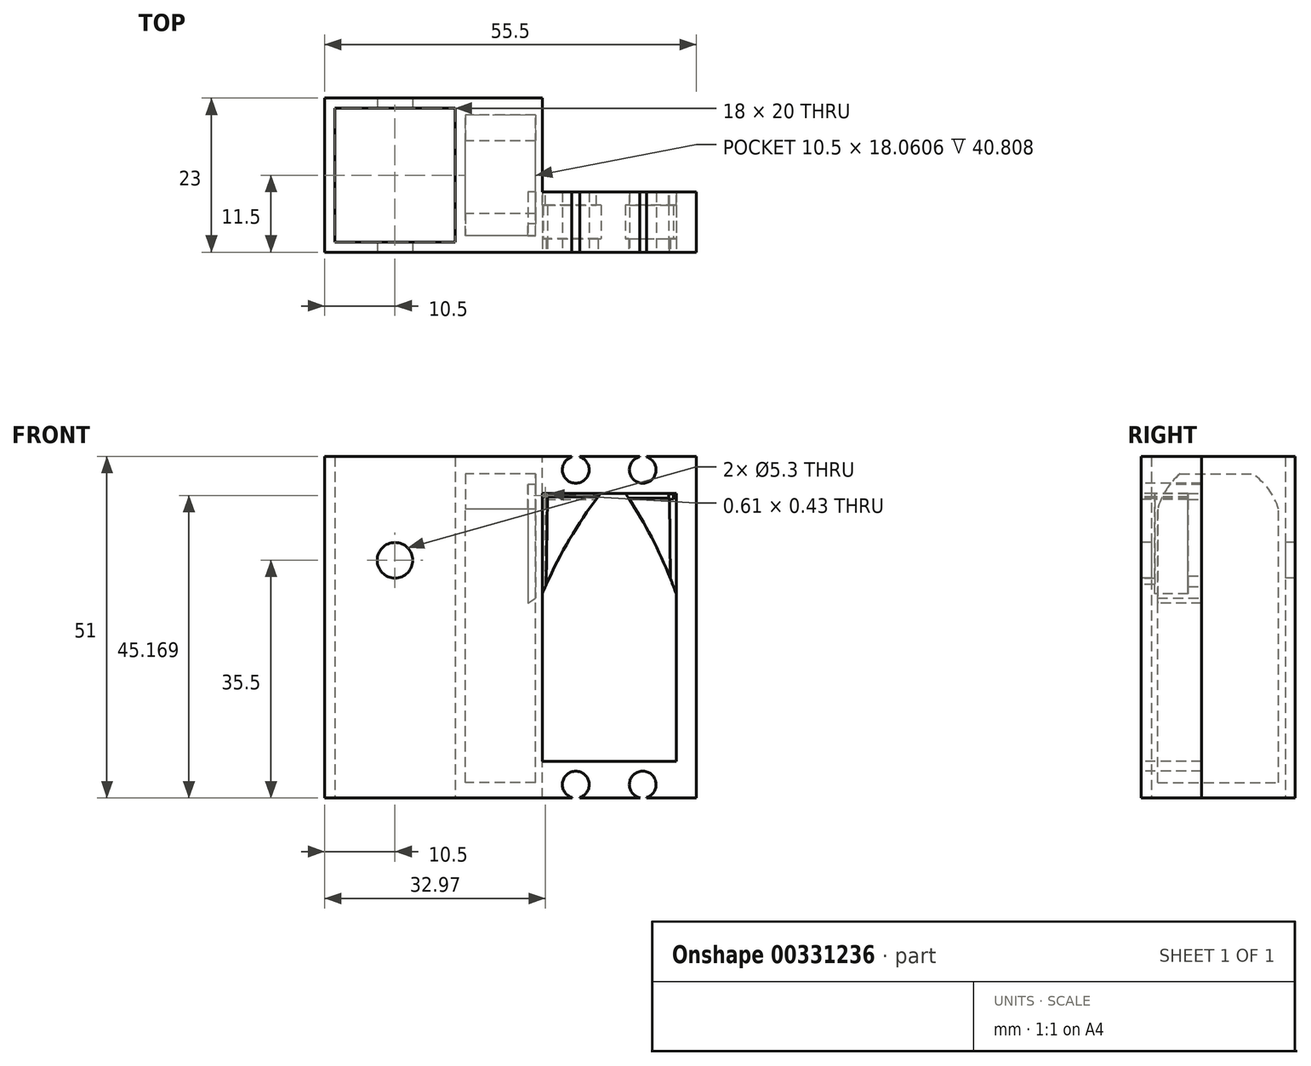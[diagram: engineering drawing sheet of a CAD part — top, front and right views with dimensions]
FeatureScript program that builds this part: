
annotation { "Feature Type Name" : "Feature", "Feature Type Description" : "" }
export const myFeature = defineFeature(function(context is Context, id is Id, definition is map)
    precondition{}
    {
        {
            var Q0;
            Q0=qCreatedBy(makeId("Top.planeOp"),FACE);
            var sketch = newSketch(context, id + "F0", { "sketchPlane" : qUnion([Q0])});
            skLineSegment(sketch, "E0.bottom", {"start": v(-9, -10) * mm, "end": v(9, -10) * mm});
            skLineSegment(sketch, "E0.top", {"start": v(-9, 10) * mm, "end": v(9, 10) * mm});
            skLineSegment(sketch, "E0.left", {"start": v(-9, -10) * mm, "end": v(-9, 10) * mm});
            skLineSegment(sketch, "E0.right", {"start": v(9, -10) * mm, "end": v(9, 10) * mm});
            skPoint(sketch, "E0.middle", {"position": v(0, 0) * mm});
            skLineSegment(sketch, "E1.bottom", {"start": v(-10.5, -11.5) * mm, "end": v(10.5, -11.5) * mm});
            skLineSegment(sketch, "E1.top", {"start": v(-10.5, 11.5) * mm, "end": v(10.5, 11.5) * mm});
            skLineSegment(sketch, "E1.left", {"start": v(-10.5, -11.5) * mm, "end": v(-10.5, 11.5) * mm});
            skLineSegment(sketch, "E1.right", {"start": v(10.5, -11.5) * mm, "end": v(10.5, 11.5) * mm});
            skSolve(sketch);
        }
        {
            var Q0;
            Q0 = qSketchRegion(id + "F0", true);
            extrude(context, id + "F1", {"entities" : qUnion([Q0]), "depth" : 51 * mm});
        }
        {
            var Q0;
            Q0=makeQuery(id+"F1.opExtrude","SWEPT_FACE",FACE,{"disambiguationData":[OSD([sQuery(id+"F0.wireOp",EDGE,"E1.right")])]});
            var sketch = newSketch(context, id + "F2", { "sketchPlane" : qUnion([Q0])});
            skLineSegment(sketch, "E2", {"start": v(-11.5, 51) * mm, "end": v(-11.5, 49) * mm});
            skLineSegment(sketch, "E3.bottom", {"start": v(-11.5, 51) * mm, "end": v(11.5, 51) * mm});
            skLineSegment(sketch, "E3.top", {"start": v(-11.5, 0) * mm, "end": v(11.5, 0) * mm});
            skLineSegment(sketch, "E3.left", {"start": v(-11.5, 51) * mm, "end": v(-11.5, 0) * mm});
            skLineSegment(sketch, "E3.right", {"start": v(11.5, 51) * mm, "end": v(11.5, 0) * mm});
            skLineSegment(sketch, "E4.bottom", {"start": v(-9.06, 2.33) * mm, "end": v(9, 2.33) * mm});
            skLineSegment(sketch, "E4.top", {"start": v(-9.06, 48.4) * mm, "end": v(9, 48.4) * mm});
            skLineSegment(sketch, "E4.left", {"start": v(-9.06, 2.33) * mm, "end": v(-9.06, 48.4) * mm});
            skLineSegment(sketch, "E4.right", {"start": v(9, 2.33) * mm, "end": v(9, 48.4) * mm});
            skArc(sketch, "E5", {"start": v(-5.75, 48.4) * mm, "mid": v(-7.8, 46) * mm, "end": v(-9.06, 43.13) * mm});
            skArc(sketch, "E6", {"start": v(9, 43.13) * mm, "mid": v(7.51, 46.1) * mm, "end": v(5.11, 48.4) * mm});
            skSolve(sketch);
        }
        {
            var Q0;
            Q0 = qSketchRegion(id + "F2", true);
            var Q1;
            {var subQ3=sQuery(id+"F2.wireOp",EDGE,"E5");Q1=makeQuery(id+"F2.imprint","IMPRINT",FACE,{"disambiguationData":[TD([[makeQuery(id+"F2.imprint","IMPRINT",EDGE,{"derivedFrom":subQ3}),-1.0]])]});}
            var Q2;
            {var subQ3=sQuery(id+"F2.wireOp",EDGE,"E6");Q2=makeQuery(id+"F2.imprint","IMPRINT",FACE,{"disambiguationData":[TD([[makeQuery(id+"F2.imprint","IMPRINT",EDGE,{"derivedFrom":subQ3}),-1.0]])]});}
            extrude(context, id + "F3", {"entities" : qUnion([Q0, Q1, Q2]), "operationType" : NewBodyOperationType.ADD, "depth" : 11.5 * mm});
        }
        {
            var Q0;
            Q0=makeQuery(id+"F3.opExtrude","CAP_FACE",FACE,{"disambiguationData":[OSD([sQuery(id+"F2.wireOp",EDGE,"E3.bottom"),sQuery(id+"F2.wireOp",EDGE,"E3.top"),sQuery(id+"F2.wireOp",EDGE,"E3.left"),sQuery(id+"F2.wireOp",EDGE,"E3.right"),sQuery(id+"F2.wireOp",EDGE,"E4.bottom"),sQuery(id+"F2.wireOp",EDGE,"E4.top"),sQuery(id+"F2.wireOp",EDGE,"E4.left"),sQuery(id+"F2.wireOp",EDGE,"E4.right"),sQuery(id+"F2.wireOp",EDGE,"E5"),sQuery(id+"F2.wireOp",EDGE,"E6")])],"isStart":false});
            var sketch = newSketch(context, id + "F4", { "sketchPlane" : qUnion([Q0])});
            skLineSegment(sketch, "E7.bottom", {"start": v(-11.5, 51) * mm, "end": v(11.5, 51) * mm});
            skLineSegment(sketch, "E7.top", {"start": v(-11.5, 0) * mm, "end": v(11.5, 0) * mm});
            skLineSegment(sketch, "E7.left", {"start": v(-11.5, 51) * mm, "end": v(-11.5, 0) * mm});
            skLineSegment(sketch, "E7.right", {"start": v(11.5, 51) * mm, "end": v(11.5, 0) * mm});
            skSolve(sketch);
        }
        {
            var Q0;
            Q0 = qSketchRegion(id + "F4", true);
            extrude(context, id + "F5", {"entities" : qUnion([Q0]), "operationType" : NewBodyOperationType.ADD, "oppositeDirection" : true, "depth" : 1 * mm});
        }
        {
            var Q0;
            Q0=makeQuery(id+"F5.boolean.opBoolean","MERGE",FACE,{"derivedFrom":[makeQuery(id+"F3.opExtrude","CAP_FACE",FACE,{"disambiguationData":[OSD([sQuery(id+"F2.wireOp",EDGE,"E3.bottom"),sQuery(id+"F2.wireOp",EDGE,"E3.top"),sQuery(id+"F2.wireOp",EDGE,"E3.left"),sQuery(id+"F2.wireOp",EDGE,"E3.right"),sQuery(id+"F2.wireOp",EDGE,"E4.bottom"),sQuery(id+"F2.wireOp",EDGE,"E4.top"),sQuery(id+"F2.wireOp",EDGE,"E4.left"),sQuery(id+"F2.wireOp",EDGE,"E4.right"),sQuery(id+"F2.wireOp",EDGE,"E5"),sQuery(id+"F2.wireOp",EDGE,"E6")])],"isStart":false}),makeQuery(id+"F5.opExtrude","CAP_FACE",FACE,{"disambiguationData":[OSD([sQuery(id+"F4.wireOp",EDGE,"E7.bottom"),sQuery(id+"F4.wireOp",EDGE,"E7.top"),sQuery(id+"F4.wireOp",EDGE,"E7.left"),sQuery(id+"F4.wireOp",EDGE,"E7.right")])],"isStart":true})]});
            var sketch = newSketch(context, id + "F6", { "sketchPlane" : qUnion([Q0])});
            skLineSegment(sketch, "E8", {"start": v(-11.5, 51) * mm, "end": v(-11.5, 49) * mm});
            skLineSegment(sketch, "E9", {"start": v(-11.5, 49) * mm, "end": v(-2.5, 49) * mm});
            skLineSegment(sketch, "E10", {"start": v(11.5, 51) * mm, "end": v(11.5, 45.5) * mm});
            skLineSegment(sketch, "E11", {"start": v(11.5, 0) * mm, "end": v(11.5, 5.5) * mm});
            skLineSegment(sketch, "E12", {"start": v(-2.5, 45.5) * mm, "end": v(-11.5, 45.5) * mm});
            skLineSegment(sketch, "E13", {"start": v(-2.5, 5.5) * mm, "end": v(-11.5, 5.5) * mm});
            skLineSegment(sketch, "E14", {"start": v(-11.5, 5.5) * mm, "end": v(-11.5, 0) * mm});
            skLineSegment(sketch, "E15", {"start": v(-11.5, 0) * mm, "end": v(11.5, 0) * mm});
            skLineSegment(sketch, "E16", {"start": v(-11.5, 45.5) * mm, "end": v(-11.5, 51) * mm});
            skLineSegment(sketch, "E17", {"start": v(-11.5, 0) * mm, "end": v(-2.5, 0) * mm});
            skLineSegment(sketch, "E18", {"start": v(-2.5, 0) * mm, "end": v(-2.5, 51) * mm});
            skLineSegment(sketch, "E19", {"start": v(-2.5, 51) * mm, "end": v(-11.5, 51) * mm});
            skLineSegment(sketch, "E20", {"start": v(-11.5, 0) * mm, "end": v(-11.5, 51) * mm});
            skLineSegment(sketch, "E21", {"start": v(-2.5, 45.5) * mm, "end": v(11.5, 45.5) * mm});
            skLineSegment(sketch, "E22", {"start": v(11.5, 51) * mm, "end": v(-2.5, 51) * mm});
            skLineSegment(sketch, "E23", {"start": v(-2.5, 5.5) * mm, "end": v(11.5, 5.5) * mm});
            skLineSegment(sketch, "E24", {"start": v(11.5, 0) * mm, "end": v(-2.5, 0) * mm});
            skSolve(sketch);
        }
        {
            var Q0;
            {var subQ0=sQuery(id+"F6.wireOp",EDGE,"E9");Q0=makeQuery(id+"F6.imprint","IMPRINT",FACE,{"disambiguationData":[TD([[makeQuery(id+"F6.imprint","IMPRINT",EDGE,{"derivedFrom":subQ0}),1.0]])]});}
            var Q1;
            {var subQ0=sQuery(id+"F6.wireOp",EDGE,"E13");Q1=makeQuery(id+"F6.imprint","IMPRINT",FACE,{"disambiguationData":[TD([[makeQuery(id+"F6.imprint","IMPRINT",EDGE,{"derivedFrom":subQ0}),1.0]])]});}
            var Q2;
            {var subQ0=sQuery(id+"F6.wireOp",EDGE,"E9");Q2=makeQuery(id+"F6.imprint","IMPRINT",FACE,{"disambiguationData":[TD([[makeQuery(id+"F6.imprint","IMPRINT",EDGE,{"derivedFrom":subQ0}),-1.0]])]});}
            var Q3;
            {var subQ0=sQuery(id+"F6.wireOp",EDGE,"E9");Q3=makeQuery(id+"F6.imprint","IMPRINT",FACE,{"disambiguationData":[TD([[makeQuery(id+"F6.imprint","IMPRINT",EDGE,{"derivedFrom":subQ0}),1.0]])]});}
            extrude(context, id + "F7", {"entities" : qUnion([Q0, Q1, Q2, Q3]), "operationType" : NewBodyOperationType.ADD, "depth" : 20 * mm});
        }
        {
            var Q0;
            Q0=makeQuery(id+"F7.opExtrude","CAP_FACE",FACE,{"disambiguationData":[OSD([sQuery(id+"F2.wireOp",EDGE,"E3.bottom"),sQuery(id+"F6.wireOp",EDGE,"E12"),sQuery(id+"F6.wireOp",EDGE,"E16"),sQuery(id+"F6.wireOp",EDGE,"E10")])],"isStart":false});
            var sketch = newSketch(context, id + "F8", { "sketchPlane" : qUnion([Q0])});
            skLineSegment(sketch, "E25.bottom", {"start": v(-2.5, 51) * mm, "end": v(11.52, 51) * mm});
            skLineSegment(sketch, "E25.top", {"start": v(-2.5, 0) * mm, "end": v(11.52, 0) * mm});
            skLineSegment(sketch, "E25.left", {"start": v(-2.5, 51) * mm, "end": v(-2.5, 0) * mm});
            skLineSegment(sketch, "E25.right", {"start": v(11.52, 51) * mm, "end": v(11.52, 0) * mm});
            skLineSegment(sketch, "E26.bottom", {"start": v(-11.5, 51) * mm, "end": v(-2.5, 51) * mm});
            skLineSegment(sketch, "E26.top", {"start": v(-11.5, 0) * mm, "end": v(-2.5, 0) * mm});
            skLineSegment(sketch, "E26.left", {"start": v(-11.5, 51) * mm, "end": v(-11.5, 0) * mm});
            skSolve(sketch);
        }
        {
            var Q0;
            {var subQ0=sQuery(id+"F8.wireOp",EDGE,"E26.bottom");Q0=makeQuery(id+"F8.imprint","IMPRINT",FACE,{"disambiguationData":[TD([[makeQuery(id+"F8.imprint","IMPRINT",EDGE,{"derivedFrom":subQ0}),-1.0]])]});}
            var Q1;
            {var subQ0=sQuery(id+"F8.wireOp",EDGE,"E26.top");Q1=makeQuery(id+"F8.imprint","IMPRINT",FACE,{"disambiguationData":[TD([[makeQuery(id+"F8.imprint","IMPRINT",EDGE,{"derivedFrom":subQ0}),1.0]])]});}
            extrude(context, id + "F9", {"entities" : qUnion([Q0, Q1]), "operationType" : NewBodyOperationType.ADD, "depth" : 3 * mm});
        }
        {
            var Q0;
            {var subQ0=sQuery(id+"F6.wireOp",EDGE,"E20");var subQ1=makeQuery(id+"F6.imprint","INTERSECT",VERTEX,{"derivedFrom":[sQuery(id+"F6.wireOp",EDGE,"E9"),subQ0]});Q0=makeQuery(id+"F9.boolean.opBoolean","MERGE",FACE,{"derivedFrom":[makeQuery(id+"F7.boolean.opBoolean","MERGE",FACE,{"derivedFrom":[makeQuery(id+"F3.boolean.opBoolean","MERGE",FACE,{"derivedFrom":[makeQuery(id+"F1.opExtrude","SWEPT_FACE",FACE,{"disambiguationData":[OSD([sQuery(id+"F0.wireOp",EDGE,"E1.bottom")])]}),makeQuery(id+"F3.opExtrude","SWEPT_FACE",FACE,{"disambiguationData":[OSD([sQuery(id+"F2.wireOp",EDGE,"E3.left")])]})]}),makeQuery(id+"F7.opExtrude","SWEPT_FACE",FACE,{"disambiguationData":[OSD([subQ0]),TDD([makeQuery(id+"F6.imprint","IMPRINT",EDGE,{"disambiguationData":[TD([[makeQuery(id+"F6.imprint","INTERSECT",VERTEX,{"derivedFrom":[sQuery(id+"F6.wireOp",EDGE,"E19"),subQ0]}),-1.0]])],"derivedFrom":subQ0}),makeQuery(id+"F6.imprint","IMPRINT",EDGE,{"disambiguationData":[TD([[subQ1,-1.0]])],"derivedFrom":subQ0})])]}),makeQuery(id+"F7.opExtrude","SWEPT_FACE",FACE,{"disambiguationData":[OSD([subQ0]),TDD([makeQuery(id+"F6.imprint","IMPRINT",EDGE,{"disambiguationData":[TD([[makeQuery(id+"F6.imprint","INTERSECT",VERTEX,{"derivedFrom":[subQ0,sQuery(id+"F6.wireOp",EDGE,"E17")]}),1.0]])],"derivedFrom":subQ0})])]})]}),makeQuery(id+"F9.opExtrude","SWEPT_FACE",FACE,{"disambiguationData":[OSD([sQuery(id+"F8.wireOp",EDGE,"E26.left")])]})]});}
            var sketch = newSketch(context, id + "F10", { "sketchPlane" : qUnion([Q0])});
            skLineSegment(sketch, "E27", {"start": v(22, 51) * mm, "end": v(22, 47) * mm});
            skLineSegment(sketch, "E28", {"start": v(22, 49) * mm, "end": v(42, 49) * mm});
            skCircle(sketch, "E29", {"center": v(37, 49) * mm, "radius": 2 * mm});
            skCircle(sketch, "E30", {"center": v(27, 49) * mm, "radius": 2 * mm});
            skPoint(sketch, "E31.orphan", {"position": v(22, 5.5) * mm});
            skPoint(sketch, "E32.end.orphan", {"position": v(22, 1.25) * mm});
            skPoint(sketch, "E33.orphan", {"position": v(22, 3.37) * mm});
            skPoint(sketch, "E34.orphan", {"position": v(32, 3.37) * mm});
            skPoint(sketch, "E35.end.orphan", {"position": v(42, 3.37) * mm});
            skLineSegment(sketch, "E36", {"start": v(22, 4) * mm, "end": v(22, 0) * mm});
            skLineSegment(sketch, "E37", {"start": v(22, 2) * mm, "end": v(42, 2) * mm});
            skCircle(sketch, "E38", {"center": v(37, 2) * mm, "radius": 2 * mm});
            skCircle(sketch, "E39", {"center": v(27, 2) * mm, "radius": 2 * mm});
            skLineSegment(sketch, "E40", {"start": v(26.42, 50.33) * mm, "end": v(26.42, 51.74) * mm});
            skLineSegment(sketch, "E41", {"start": v(26.42, 51.74) * mm, "end": v(27.57, 51.74) * mm});
            skLineSegment(sketch, "E42", {"start": v(27.57, 51.74) * mm, "end": v(27.57, 50.5) * mm});
            skLineSegment(sketch, "E43", {"start": v(36.57, 50.41) * mm, "end": v(36.57, 52.17) * mm});
            skLineSegment(sketch, "E44", {"start": v(36.57, 52.17) * mm, "end": v(37.6, 52.17) * mm});
            skLineSegment(sketch, "E45", {"start": v(37.6, 52.17) * mm, "end": v(37.6, 50.41) * mm});
            skLineSegment(sketch, "E46", {"start": v(37.55, 0.67) * mm, "end": v(37.55, -1.47) * mm});
            skLineSegment(sketch, "E47", {"start": v(37.55, -1.47) * mm, "end": v(36.62, -1.47) * mm});
            skLineSegment(sketch, "E48", {"start": v(36.62, -1.47) * mm, "end": v(36.62, 1) * mm});
            skLineSegment(sketch, "E49", {"start": v(27.57, 0.83) * mm, "end": v(27.57, -2.08) * mm});
            skLineSegment(sketch, "E50", {"start": v(27.57, -2.08) * mm, "end": v(26.44, -2.08) * mm});
            skLineSegment(sketch, "E51", {"start": v(26.44, -2.08) * mm, "end": v(26.44, 0.92) * mm});
            skSolve(sketch);
        }
        {
            var Q0;
            Q0 = qSketchRegion(id + "F10", true);
            extrude(context, id + "F11", {"entities" : qUnion([Q0]), "operationType" : NewBodyOperationType.REMOVE, "oppositeDirection" : true, "depth" : 25 * mm});
        }
        {
            var Q0;
            {var subQ0=sQuery(id+"F6.wireOp",EDGE,"E20");var subQ1=makeQuery(id+"F6.imprint","INTERSECT",VERTEX,{"derivedFrom":[sQuery(id+"F6.wireOp",EDGE,"E9"),subQ0]});Q0=makeQuery(id+"F9.boolean.opBoolean","MERGE",FACE,{"derivedFrom":[makeQuery(id+"F7.boolean.opBoolean","MERGE",FACE,{"derivedFrom":[makeQuery(id+"F3.boolean.opBoolean","MERGE",FACE,{"derivedFrom":[makeQuery(id+"F1.opExtrude","SWEPT_FACE",FACE,{"disambiguationData":[OSD([sQuery(id+"F0.wireOp",EDGE,"E1.bottom")])]}),makeQuery(id+"F3.opExtrude","SWEPT_FACE",FACE,{"disambiguationData":[OSD([sQuery(id+"F2.wireOp",EDGE,"E3.left")])]})]}),makeQuery(id+"F7.opExtrude","SWEPT_FACE",FACE,{"disambiguationData":[OSD([subQ0]),TDD([makeQuery(id+"F6.imprint","IMPRINT",EDGE,{"disambiguationData":[TD([[makeQuery(id+"F6.imprint","INTERSECT",VERTEX,{"derivedFrom":[sQuery(id+"F6.wireOp",EDGE,"E19"),subQ0]}),-1.0]])],"derivedFrom":subQ0}),makeQuery(id+"F6.imprint","IMPRINT",EDGE,{"disambiguationData":[TD([[subQ1,-1.0]])],"derivedFrom":subQ0})])]}),makeQuery(id+"F7.opExtrude","SWEPT_FACE",FACE,{"disambiguationData":[OSD([subQ0]),TDD([makeQuery(id+"F6.imprint","IMPRINT",EDGE,{"disambiguationData":[TD([[makeQuery(id+"F6.imprint","INTERSECT",VERTEX,{"derivedFrom":[subQ0,sQuery(id+"F6.wireOp",EDGE,"E17")]}),1.0]])],"derivedFrom":subQ0})])]})]}),makeQuery(id+"F9.opExtrude","SWEPT_FACE",FACE,{"disambiguationData":[OSD([sQuery(id+"F8.wireOp",EDGE,"E26.left")])]})]});}
            var sketch = newSketch(context, id + "F12", { "sketchPlane" : qUnion([Q0])});
            skLineSegment(sketch, "E52", {"start": v(-10.5, 51) * mm, "end": v(0, 51) * mm});
            skLineSegment(sketch, "E53", {"start": v(22, 45.5) * mm, "end": v(0, 45.5) * mm});
            skLineSegment(sketch, "E54", {"start": v(0, 45.5) * mm, "end": v(0, 35.5) * mm});
            skCircle(sketch, "E55", {"center": v(0, 35.5) * mm, "radius": 2.65 * mm});
            skSolve(sketch);
        }
        {
            var Q0;
            Q0 = qSketchRegion(id + "F12", true);
            extrude(context, id + "F13", {"entities" : qUnion([Q0]), "operationType" : NewBodyOperationType.REMOVE, "oppositeDirection" : true, "depth" : 25 * mm});
        }
        {
            var Q0;
            {var subQ0=sQuery(id+"F6.wireOp",EDGE,"E20");var subQ1=makeQuery(id+"F6.imprint","INTERSECT",VERTEX,{"derivedFrom":[sQuery(id+"F6.wireOp",EDGE,"E9"),subQ0]});Q0=makeQuery(id+"F9.boolean.opBoolean","MERGE",FACE,{"derivedFrom":[makeQuery(id+"F7.boolean.opBoolean","MERGE",FACE,{"derivedFrom":[makeQuery(id+"F3.boolean.opBoolean","MERGE",FACE,{"derivedFrom":[makeQuery(id+"F1.opExtrude","SWEPT_FACE",FACE,{"disambiguationData":[OSD([sQuery(id+"F0.wireOp",EDGE,"E1.bottom")])]}),makeQuery(id+"F3.opExtrude","SWEPT_FACE",FACE,{"disambiguationData":[OSD([sQuery(id+"F2.wireOp",EDGE,"E3.left")])]})]}),makeQuery(id+"F7.opExtrude","SWEPT_FACE",FACE,{"disambiguationData":[OSD([subQ0]),TDD([makeQuery(id+"F6.imprint","IMPRINT",EDGE,{"disambiguationData":[TD([[makeQuery(id+"F6.imprint","INTERSECT",VERTEX,{"derivedFrom":[sQuery(id+"F6.wireOp",EDGE,"E19"),subQ0]}),-1.0]])],"derivedFrom":subQ0}),makeQuery(id+"F6.imprint","IMPRINT",EDGE,{"disambiguationData":[TD([[subQ1,-1.0]])],"derivedFrom":subQ0})])]}),makeQuery(id+"F7.opExtrude","SWEPT_FACE",FACE,{"disambiguationData":[OSD([subQ0]),TDD([makeQuery(id+"F6.imprint","IMPRINT",EDGE,{"disambiguationData":[TD([[makeQuery(id+"F6.imprint","INTERSECT",VERTEX,{"derivedFrom":[subQ0,sQuery(id+"F6.wireOp",EDGE,"E17")]}),1.0]])],"derivedFrom":subQ0})])]})]}),makeQuery(id+"F9.opExtrude","SWEPT_FACE",FACE,{"disambiguationData":[OSD([sQuery(id+"F8.wireOp",EDGE,"E26.left")])]})]});}
            var sketch = newSketch(context, id + "F14", { "sketchPlane" : qUnion([Q0])});
            skArc(sketch, "E56", {"start": v(30.75, 45.5) * mm, "mid": v(25.87, 38.28) * mm, "end": v(22, 30.47) * mm});
            skArc(sketch, "E57", {"start": v(42, 30.47) * mm, "mid": v(38.67, 38.22) * mm, "end": v(34.4, 45.5) * mm});
            skLineSegment(sketch, "E58", {"start": v(30.75, 45.5) * mm, "end": v(30.75, 46.8) * mm});
            skLineSegment(sketch, "E59", {"start": v(30.75, 46.8) * mm, "end": v(19.84, 46.8) * mm});
            skLineSegment(sketch, "E60", {"start": v(19.84, 46.8) * mm, "end": v(19.84, 29.1) * mm});
            skLineSegment(sketch, "E61", {"start": v(19.84, 29.1) * mm, "end": v(22, 30.47) * mm});
            skLineSegment(sketch, "E62", {"start": v(34.4, 45.5) * mm, "end": v(42.57, 46.8) * mm});
            skPoint(sketch, "E62.endSnap0", {"position": v(25.3, 46.8) * mm});
            skLineSegment(sketch, "E63", {"start": v(42.57, 46.8) * mm, "end": v(44.02, 42.14) * mm});
            skLineSegment(sketch, "E64", {"start": v(44.02, 42.14) * mm, "end": v(42, 30.47) * mm});
            skSolve(sketch);
        }
        {
            var Q0;
            Q0 = qSketchRegion(id + "F14", true);
            extrude(context, id + "F15", {"entities" : qUnion([Q0]), "operationType" : NewBodyOperationType.ADD, "oppositeDirection" : true, "depth" : 9 * mm});
        }
        {
            var Q0;
            {var subQ0=sQuery(id+"F6.wireOp",EDGE,"E20");var subQ1=makeQuery(id+"F6.imprint","INTERSECT",VERTEX,{"derivedFrom":[sQuery(id+"F6.wireOp",EDGE,"E9"),subQ0]});Q0=makeQuery(id+"F15.boolean.opBoolean","MERGE",FACE,{"derivedFrom":[makeQuery(id+"F9.boolean.opBoolean","MERGE",FACE,{"derivedFrom":[makeQuery(id+"F7.boolean.opBoolean","MERGE",FACE,{"derivedFrom":[makeQuery(id+"F3.boolean.opBoolean","MERGE",FACE,{"derivedFrom":[makeQuery(id+"F1.opExtrude","SWEPT_FACE",FACE,{"disambiguationData":[OSD([sQuery(id+"F0.wireOp",EDGE,"E1.bottom")])]}),makeQuery(id+"F3.opExtrude","SWEPT_FACE",FACE,{"disambiguationData":[OSD([sQuery(id+"F2.wireOp",EDGE,"E3.left")])]})]}),makeQuery(id+"F7.opExtrude","SWEPT_FACE",FACE,{"disambiguationData":[OSD([subQ0]),TDD([makeQuery(id+"F6.imprint","IMPRINT",EDGE,{"disambiguationData":[TD([[makeQuery(id+"F6.imprint","INTERSECT",VERTEX,{"derivedFrom":[sQuery(id+"F6.wireOp",EDGE,"E19"),subQ0]}),-1.0]])],"derivedFrom":subQ0}),makeQuery(id+"F6.imprint","IMPRINT",EDGE,{"disambiguationData":[TD([[subQ1,-1.0]])],"derivedFrom":subQ0})])]}),makeQuery(id+"F7.opExtrude","SWEPT_FACE",FACE,{"disambiguationData":[OSD([subQ0]),TDD([makeQuery(id+"F6.imprint","IMPRINT",EDGE,{"disambiguationData":[TD([[makeQuery(id+"F6.imprint","INTERSECT",VERTEX,{"derivedFrom":[subQ0,sQuery(id+"F6.wireOp",EDGE,"E17")]}),1.0]])],"derivedFrom":subQ0})])]})]}),makeQuery(id+"F9.opExtrude","SWEPT_FACE",FACE,{"disambiguationData":[OSD([sQuery(id+"F8.wireOp",EDGE,"E26.left")])]})]}),makeQuery(id+"F15.opExtrude","CAP_FACE",FACE,{"disambiguationData":[OSD([sQuery(id+"F14.wireOp",EDGE,"E56"),sQuery(id+"F14.wireOp",EDGE,"E58"),sQuery(id+"F14.wireOp",EDGE,"E59"),sQuery(id+"F14.wireOp",EDGE,"E60"),sQuery(id+"F14.wireOp",EDGE,"E61")])],"isStart":true}),makeQuery(id+"F15.opExtrude","CAP_FACE",FACE,{"disambiguationData":[OSD([sQuery(id+"F14.wireOp",EDGE,"E57"),sQuery(id+"F14.wireOp",EDGE,"E62"),sQuery(id+"F14.wireOp",EDGE,"E63"),sQuery(id+"F14.wireOp",EDGE,"E64")])],"isStart":true})]});}
            var sketch = newSketch(context, id + "F16", { "sketchPlane" : qUnion([Q0])});
            skLineSegment(sketch, "E65", {"start": v(22, 30.47) * mm, "end": v(22, 45.5) * mm});
            skLineSegment(sketch, "E66", {"start": v(22, 45.5) * mm, "end": v(30.75, 45.5) * mm});
            skLineSegment(sketch, "E67", {"start": v(30.75, 45.5) * mm, "end": v(30.33, 44.95) * mm});
            skLineSegment(sketch, "E68", {"start": v(30.33, 44.95) * mm, "end": v(22.77, 44.95) * mm});
            skLineSegment(sketch, "E69", {"start": v(22.77, 44.95) * mm, "end": v(22.6, 31.9) * mm});
            skLineSegment(sketch, "E70", {"start": v(22.6, 31.9) * mm, "end": v(22, 30.47) * mm});
            skLineSegment(sketch, "E71", {"start": v(34.4, 45.5) * mm, "end": v(42, 45.5) * mm});
            skLineSegment(sketch, "E72", {"start": v(42, 45.5) * mm, "end": v(42, 30.47) * mm});
            skLineSegment(sketch, "E73", {"start": v(42, 30.47) * mm, "end": v(41.64, 31.46) * mm});
            skLineSegment(sketch, "E74", {"start": v(34.9, 44.76) * mm, "end": v(41.01, 44.76) * mm});
            skLineSegment(sketch, "E75", {"start": v(41.01, 44.76) * mm, "end": v(41.13, 32.77) * mm});
            skLineSegment(sketch, "E76", {"start": v(41.13, 32.77) * mm, "end": v(42, 30.47) * mm});
            skLineSegment(sketch, "E77", {"start": v(42, 30.47) * mm, "end": v(41.13, 32.77) * mm});
            skSolve(sketch);
        }
        {
            var Q0;
            Q0 = qSketchRegion(id + "F16", true);
            var Q1;
            {var subQ7=sQuery(id+"F16.wireOp",EDGE,"E71");Q1=makeQuery(id+"F16.imprint","IMPRINT",FACE,{"disambiguationData":[TD([[makeQuery(id+"F16.imprint","IMPRINT",EDGE,{"derivedFrom":subQ7}),-1.0]])]});}
            extrude(context, id + "F17", {"entities" : qUnion([Q0, Q1]), "operationType" : NewBodyOperationType.REMOVE, "oppositeDirection" : true, "depth" : 2 * mm});
        }
        {
            var Q0;
            {var subQ0=sQuery(id+"F6.wireOp",EDGE,"E18");var subQ1=makeQuery(id+"F6.imprint","INTERSECT",VERTEX,{"derivedFrom":[sQuery(id+"F6.wireOp",EDGE,"E9"),subQ0]});Q0=makeQuery(id+"F15.boolean.opBoolean","MERGE",FACE,{"derivedFrom":[makeQuery(id+"F9.boolean.opBoolean","MERGE",FACE,{"derivedFrom":[makeQuery(id+"F7.opExtrude","SWEPT_FACE",FACE,{"disambiguationData":[OSD([subQ0]),TDD([makeQuery(id+"F6.imprint","IMPRINT",EDGE,{"disambiguationData":[TD([[makeQuery(id+"F6.imprint","INTERSECT",VERTEX,{"derivedFrom":[sQuery(id+"F6.wireOp",EDGE,"E13"),subQ0,sQuery(id+"F6.wireOp",EDGE,"E23")]}),1.0]])],"derivedFrom":subQ0})])]}),makeQuery(id+"F7.opExtrude","SWEPT_FACE",FACE,{"disambiguationData":[OSD([subQ0]),TDD([makeQuery(id+"F6.imprint","IMPRINT",EDGE,{"disambiguationData":[TD([[subQ1,1.0]])],"derivedFrom":subQ0}),makeQuery(id+"F6.imprint","IMPRINT",EDGE,{"disambiguationData":[TD([[subQ1,-1.0]])],"derivedFrom":subQ0})])]}),makeQuery(id+"F9.opExtrude","SWEPT_FACE",FACE,{"disambiguationData":[OSD([sQuery(id+"F8.wireOp",EDGE,"E25.left")])]})]}),makeQuery(id+"F15.opExtrude","CAP_FACE",FACE,{"disambiguationData":[OSD([sQuery(id+"F14.wireOp",EDGE,"E56"),sQuery(id+"F14.wireOp",EDGE,"E58"),sQuery(id+"F14.wireOp",EDGE,"E59"),sQuery(id+"F14.wireOp",EDGE,"E60"),sQuery(id+"F14.wireOp",EDGE,"E61")])],"isStart":false}),makeQuery(id+"F15.opExtrude","CAP_FACE",FACE,{"disambiguationData":[OSD([sQuery(id+"F14.wireOp",EDGE,"E57"),sQuery(id+"F14.wireOp",EDGE,"E62"),sQuery(id+"F14.wireOp",EDGE,"E63"),sQuery(id+"F14.wireOp",EDGE,"E64")])],"isStart":false})]});}
            var sketch = newSketch(context, id + "F18", { "sketchPlane" : qUnion([Q0])});
            skLineSegment(sketch, "E78", {"start": v(-42, 30.47) * mm, "end": v(-42, 45.5) * mm});
            skLineSegment(sketch, "E79", {"start": v(-42, 45.5) * mm, "end": v(-34.4, 45.5) * mm});
            skLineSegment(sketch, "E80", {"start": v(-34.4, 45.5) * mm, "end": v(-35.02, 44.57) * mm});
            skLineSegment(sketch, "E81", {"start": v(-35.02, 44.57) * mm, "end": v(-40.88, 44.57) * mm});
            skLineSegment(sketch, "E82", {"start": v(-40.88, 44.57) * mm, "end": v(-40.97, 33.15) * mm});
            skLineSegment(sketch, "E83", {"start": v(-40.97, 33.15) * mm, "end": v(-42, 30.47) * mm});
            skLineSegment(sketch, "E84", {"start": v(-30.75, 45.5) * mm, "end": v(-22, 45.5) * mm});
            skPoint(sketch, "E84.endSnap0", {"position": v(-22, 40.74) * mm});
            skLineSegment(sketch, "E85", {"start": v(-22, 45.5) * mm, "end": v(-22, 30.47) * mm});
            skLineSegment(sketch, "E86", {"start": v(-22, 30.47) * mm, "end": v(-22.46, 31.56) * mm});
            skLineSegment(sketch, "E87", {"start": v(-22.46, 31.56) * mm, "end": v(-22.46, 44.6) * mm});
            skLineSegment(sketch, "E88", {"start": v(-22.46, 44.6) * mm, "end": v(-30.06, 44.6) * mm});
            skSolve(sketch);
        }
        {
            var Q0;
            Q0 = qSketchRegion(id + "F18", true);
            var Q1;
            {var subQ3=sQuery(id+"F18.wireOp",EDGE,"E84");Q1=makeQuery(id+"F18.imprint","IMPRINT",FACE,{"disambiguationData":[TD([[makeQuery(id+"F18.imprint","IMPRINT",EDGE,{"derivedFrom":subQ3}),-1.0]])]});}
            extrude(context, id + "F19", {"entities" : qUnion([Q0, Q1]), "operationType" : NewBodyOperationType.REMOVE, "oppositeDirection" : true, "depth" : 2 * mm});
        }
        {
            var Q0;
            {var subQ0=sQuery(id+"F14.wireOp",EDGE,"E56");var subQ1=sQuery(id+"F6.wireOp",EDGE,"E20");var subQ2=makeQuery(id+"F6.imprint","INTERSECT",VERTEX,{"derivedFrom":[sQuery(id+"F6.wireOp",EDGE,"E9"),subQ1]});Q0=makeQuery(id+"F17.boolean.opBoolean","SPLIT",FACE,{"disambiguationData":[TD([makeQuery(id+"F15.opExtrude","SWEPT_FACE",FACE,{"disambiguationData":[OSD([subQ0])]})])],"derivedFrom":makeQuery(id+"F15.boolean.opBoolean","MERGE",FACE,{"derivedFrom":[makeQuery(id+"F9.boolean.opBoolean","MERGE",FACE,{"derivedFrom":[makeQuery(id+"F7.boolean.opBoolean","MERGE",FACE,{"derivedFrom":[makeQuery(id+"F3.boolean.opBoolean","MERGE",FACE,{"derivedFrom":[makeQuery(id+"F1.opExtrude","SWEPT_FACE",FACE,{"disambiguationData":[OSD([sQuery(id+"F0.wireOp",EDGE,"E1.bottom")])]}),makeQuery(id+"F3.opExtrude","SWEPT_FACE",FACE,{"disambiguationData":[OSD([sQuery(id+"F2.wireOp",EDGE,"E3.left")])]})]}),makeQuery(id+"F7.opExtrude","SWEPT_FACE",FACE,{"disambiguationData":[OSD([subQ1]),TDD([makeQuery(id+"F6.imprint","IMPRINT",EDGE,{"disambiguationData":[TD([[makeQuery(id+"F6.imprint","INTERSECT",VERTEX,{"derivedFrom":[sQuery(id+"F6.wireOp",EDGE,"E19"),subQ1]}),-1.0]])],"derivedFrom":subQ1}),makeQuery(id+"F6.imprint","IMPRINT",EDGE,{"disambiguationData":[TD([[subQ2,-1.0]])],"derivedFrom":subQ1})])]}),makeQuery(id+"F7.opExtrude","SWEPT_FACE",FACE,{"disambiguationData":[OSD([subQ1]),TDD([makeQuery(id+"F6.imprint","IMPRINT",EDGE,{"disambiguationData":[TD([[makeQuery(id+"F6.imprint","INTERSECT",VERTEX,{"derivedFrom":[subQ1,sQuery(id+"F6.wireOp",EDGE,"E17")]}),1.0]])],"derivedFrom":subQ1})])]})]}),makeQuery(id+"F9.opExtrude","SWEPT_FACE",FACE,{"disambiguationData":[OSD([sQuery(id+"F8.wireOp",EDGE,"E26.left")])]})]}),makeQuery(id+"F15.opExtrude","CAP_FACE",FACE,{"disambiguationData":[OSD([subQ0,sQuery(id+"F14.wireOp",EDGE,"E58"),sQuery(id+"F14.wireOp",EDGE,"E59"),sQuery(id+"F14.wireOp",EDGE,"E60"),sQuery(id+"F14.wireOp",EDGE,"E61")])],"isStart":true}),makeQuery(id+"F15.opExtrude","CAP_FACE",FACE,{"disambiguationData":[OSD([sQuery(id+"F14.wireOp",EDGE,"E57"),sQuery(id+"F14.wireOp",EDGE,"E62"),sQuery(id+"F14.wireOp",EDGE,"E63"),sQuery(id+"F14.wireOp",EDGE,"E64")])],"isStart":true})]})});}
            var sketch = newSketch(context, id + "F20", { "sketchPlane" : qUnion([Q0])});
            skLineSegment(sketch, "E89", {"start": v(22.77, 44.95) * mm, "end": v(22.17, 44.96) * mm});
            skLineSegment(sketch, "E90", {"start": v(22.17, 44.96) * mm, "end": v(22.17, 45.38) * mm});
            skLineSegment(sketch, "E91", {"start": v(22.17, 45.38) * mm, "end": v(22.77, 45.38) * mm});
            skLineSegment(sketch, "E92", {"start": v(22.77, 45.38) * mm, "end": v(22.77, 44.95) * mm});
            skLineSegment(sketch, "E93", {"start": v(40.86, 44.7) * mm, "end": v(40.86, 45.38) * mm});
            skLineSegment(sketch, "E94", {"start": v(40.86, 45.38) * mm, "end": v(41.57, 45.38) * mm});
            skLineSegment(sketch, "E95", {"start": v(41.57, 45.38) * mm, "end": v(41.57, 44.58) * mm});
            skLineSegment(sketch, "E96", {"start": v(41.57, 44.58) * mm, "end": v(40.86, 44.7) * mm});
            skSolve(sketch);
        }
        {
            var Q0;
            Q0 = qSketchRegion(id + "F20", true);
            extrude(context, id + "F21", {"entities" : qUnion([Q0]), "operationType" : NewBodyOperationType.REMOVE, "oppositeDirection" : true, "depth" : 25 * mm});
        }
    });
